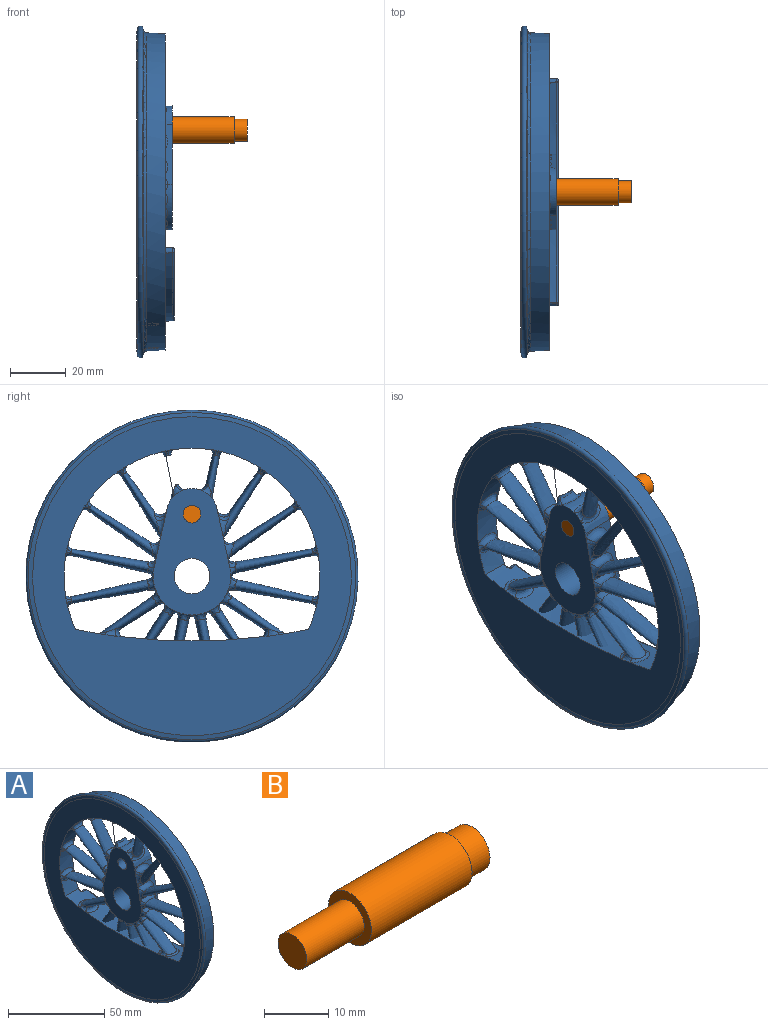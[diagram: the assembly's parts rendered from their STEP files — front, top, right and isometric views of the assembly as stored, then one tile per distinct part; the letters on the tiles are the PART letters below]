
ASSEMBLY  parts=2 mates=1
PART A: 135 faces, bbox 15.7x129.4x129.4 mm
  f0: cone r=9.16mm half-angle=2deg, axis (-1,0,0), area 176.3mm2, adj f1,f4,f129,f132,f133,f134
  f1: bspline ~10.76x6.08mm, area 60.7mm2, adj f0,f2,f3
  f2: bspline ~6.76x4.39mm, area 3.4mm2, adj f1,f3
  f3: bspline ~4.75x4.08mm, area 8.3mm2, adj f1,f2,f134
  f4: plane 21.3x12.7mm, normal (0.03,0.98,0.21), area 56.8mm2, adj f0,f5,f126,f127,f128,f129,f134
  f5: bspline ~11.82x11.44mm, area 83.1mm2, adj f4,f6,f7,f8,f9,f126
  f6: bspline ~4.14x3.37mm, area 6.3mm2, adj f5,f8,f9,f134
  f7: plane 1.45x1.08mm, normal (0.03,0.98,0.21), area 0.7mm2, adj f5,f126,f134
  f8: bspline ~6.9x3.29mm, area 11.8mm2, adj f5,f6,f9,f134
  f9: bspline ~23.53x17.18mm, area 361.5mm2, adj f5,f6,f8,f10,f125
  f10: bspline ~9.89x5.25mm, area 51.6mm2, adj f9,f11,f125
  f11: cone r=45.91mm half-angle=2deg, axis (1,0,0), area 1324.9mm2, adj f10,f12,f16,f19,f86,f87,f88,f112
  f12: bspline ~9.69x6.17mm, area 51.6mm2, adj f11,f13,f15
  f13: bspline ~15.19x7.22mm, area 197.8mm2, adj f12,f14,f15,f133
  f14: bspline ~4.75x4.08mm, area 8.3mm2, adj f13,f133,f134
  f15: bspline ~2.37x2.08mm, area 3.2mm2, adj f12,f13,f123
  f16: bspline ~9.69x6.17mm, area 51.6mm2, adj f11,f17,f18
  f17: bspline ~2.79x2.16mm, area 3.2mm2, adj f16,f18,f123
  f18: bspline ~6.39x2.51mm, area 1.6mm2, adj f16,f17
  f19: bspline ~9.89x5.24mm, area 51.6mm2, adj f11,f20,f21
  f20: bspline ~2.34x2.25mm, area 3.2mm2, adj f19,f21,f123
  f21: bspline ~25.72x18.68mm, area 455.8mm2, adj f19,f20,f22,f126
  f22: bspline ~7.22x3.59mm, area 11.9mm2, adj f21,f23,f126,f127,f134
  f23: bspline ~3.58x2.9mm, area 4.7mm2, adj f22,f24,f85,f127,f134
  f24: bspline ~28.93x8.8mm, area 483.4mm2, adj f23,f25,f84,f85,f86,f127
  f25: bspline ~11.52x4.62mm, area 34.3mm2, adj f24,f26,f85,f127,f128
  f26: bspline ~11.17x7.51mm, area 67.4mm2, adj f25,f27,f29,f83,f128
  f27: bspline ~28.93x8.8mm, area 486.9mm2, adj f26,f28,f83,f87
  f28: bspline ~2.37x2.08mm, area 3.2mm2, adj f27,f87,f123
  f29: bspline ~11.93x6.38mm, area 67.4mm2, adj f26,f30,f34,f82,f128
  f30: bspline ~21.12x15.67mm, area 345.6mm2, adj f29,f31,f32,f33,f82
  f31: bspline ~9.94x9.73mm, area 61.2mm2, adj f30,f32,f33,f119
  f32: bspline ~31.33x21.72mm, area 0mm2, adj f30,f31
  f33: bspline ~5.64x2.95mm, area 9.5mm2, adj f30,f31,f123
  f34: bspline ~11.68x6.38mm, area 67.4mm2, adj f29,f35,f80,f81,f128
  f35: bspline ~36.2x25.52mm, area 664.1mm2, adj f34,f36,f77,f81
  f36: cone r=56.77mm half-angle=2.8deg, axis (-1,0,0), area 6mm2, adj f35,f37
  f37: torus R=58.49mm, axis (-1,0,0), area 680mm2, adj f36,f38,f72,f73,f74,f77
  f38: cone r=56.77mm half-angle=2.8deg, axis (-1,0,0), area 6mm2, adj f37,f39
  f39: bspline ~41.37x10.96mm, area 664.1mm2, adj f38,f40,f77,f80
  f40: bspline ~5.5x3.18mm, area 8.8mm2, adj f39,f41,f80,f81,f134
  f41: bspline ~5.5x3.18mm, area 8.8mm2, adj f40,f42,f43,f71,f134
  f42: bspline ~41.37x10.96mm, area 664.1mm2, adj f41,f43,f72,f77
  f43: bspline ~11.68x7.51mm, area 67.4mm2, adj f41,f42,f44,f80,f128
  f44: bspline ~11.68x6.38mm, area 67.4mm2, adj f43,f45,f46,f71,f128
  f45: bspline ~36.2x25.52mm, area 664.1mm2, adj f44,f71,f73,f77
  f46: bspline ~11.93x6.38mm, area 67.4mm2, adj f44,f47,f50,f70,f128
  f47: bspline ~21.1x15.65mm, area 345.5mm2, adj f46,f48,f49,f70
  f48: bspline ~9.94x9.73mm, area 61.2mm2, adj f47,f49,f119
  f49: bspline ~5.29x2.96mm, area 9.5mm2, adj f47,f48,f123
  f50: bspline ~11.93x7.51mm, area 67.4mm2, adj f46,f51,f53,f69,f128
  f51: bspline ~28.93x8.8mm, area 486.9mm2, adj f50,f52,f69,f120
  f52: bspline ~2.79x2.11mm, area 3.2mm2, adj f51,f120,f123
  f53: bspline ~11.52x4.62mm, area 34.3mm2, adj f50,f54,f67,f68,f128
  f54: bspline ~28.93x8.8mm, area 483.4mm2, adj f53,f55,f66,f67,f68,f121
  f55: bspline ~3.58x2.9mm, area 4.7mm2, adj f54,f56,f67,f68,f134
  f56: bspline ~7.15x3.59mm, area 11.9mm2, adj f55,f57,f59,f68,f134
  f57: bspline ~25.72x18.68mm, area 455.7mm2, adj f56,f58,f59,f122
  f58: bspline ~2.34x2.25mm, area 3.2mm2, adj f57,f122,f123
  f59: bspline ~11.81x9.42mm, area 67.9mm2, adj f56,f57,f60,f65,f68,f132
  f60: bspline ~11.82x11.61mm, area 83.1mm2, adj f59,f61,f62,f63,f65,f132
  f61: bspline ~6.68x3.27mm, area 11.8mm2, adj f60,f62,f63,f134
  f62: bspline ~4.14x3.37mm, area 6.3mm2, adj f60,f61,f63,f134
  f63: bspline ~23.53x17.18mm, area 361.4mm2, adj f60,f61,f62,f64,f124
  f64: bspline ~2.54x2.44mm, area 3.2mm2, adj f63,f123,f124
  f65: plane 1.45x1.08mm, normal (0.03,-0.98,0.21), area 0.7mm2, adj f59,f60,f134
  f66: bspline ~2.37x2.08mm, area 3.2mm2, adj f54,f121,f123
  f67: bspline ~3.26x2.41mm, area 4.8mm2, adj f53,f54,f55,f69,f134
  f68: bspline ~11.75x4.6mm, area 29.7mm2, adj f53,f54,f55,f56,f59,f132
  f69: bspline ~5.5x3.18mm, area 8.8mm2, adj f50,f51,f67,f70,f134
  f70: bspline ~4.7x4.25mm, area 8.8mm2, adj f46,f47,f69,f71,f134
  f71: bspline ~4.7x4.25mm, area 8.8mm2, adj f41,f44,f45,f70,f134
  f72: cone r=56.77mm half-angle=2.8deg, axis (-1,0,0), area 6mm2, adj f37,f42
  f73: cone r=56.77mm half-angle=2.8deg, axis (-1,0,0), area 6mm2, adj f37,f45
  f74: cone r=58.25mm half-angle=80deg, axis (-1,0,0), area 168mm2, adj f37,f75
  f75: torus R=58.52mm, axis (-1,0,0), area 1056mm2, adj f74,f76
  f76: cone r=57.15mm half-angle=80deg, axis (1,0,0), area 572.1mm2, adj f75,f123
  f77: cone r=56.77mm half-angle=2.8deg, axis (-1,0,0), area 2387.5mm2, adj f35,f37,f39,f42,f45,f78
  f78: plane 113.53x113.53mm, normal (1,0,0), area 2217.4mm2, adj f77,f79
  f79: cylinder r=50.16mm len=100.33mm, axis (-1,0,0), area 128.1mm2, adj f78,f114
  f80: bspline ~11.68x7.52mm, area 67.4mm2, adj f34,f39,f40,f43,f128
  f81: bspline ~4.7x4.25mm, area 8.8mm2, adj f34,f35,f40,f82,f134
  f82: bspline ~4.7x4.25mm, area 8.8mm2, adj f29,f30,f81,f83,f134
  f83: bspline ~5.5x3.18mm, area 8.8mm2, adj f26,f27,f82,f85,f134
  f84: bspline ~2.79x2.11mm, area 3.2mm2, adj f24,f86,f123
  f85: bspline ~3.26x2.41mm, area 4.8mm2, adj f23,f24,f25,f83,f134
  f86: bspline ~9.89x6.18mm, area 51.6mm2, adj f11,f24,f84
  f87: bspline ~9.89x6.18mm, area 51.6mm2, adj f11,f27,f28
  f88: torus R=203.57mm, axis (1,0,0), area 1mm2, adj f11,f89,f111,f112,f119
  f89: plane 0.9x0.88mm, normal (1,0,0), area 0.3mm2, adj f88,f90,f112
  f90: torus R=2.1mm, axis (1,0,0), area 1.5mm2, adj f89,f91,f110,f111,f113
  f91: cylinder r=1.59mm len=2.57mm, axis (-1,0,0), area 6.6mm2, adj f90,f92,f108,f109
  f92: bspline ~4.2x0.69mm, area 0.4mm2, adj f91,f93,f110,f115
  f93: sphere r=0.51mm, area 0.1mm2, adj f92,f94,f108
  f94: torus R=45.64mm, axis (1,0,0), area 77.5mm2, adj f93,f95,f107,f115
  f95: sphere r=0.51mm, area 0.1mm2, adj f94,f96,f106
  f96: torus R=1.08mm, axis (1,0,0), area 1.3mm2, adj f95,f97,f103,f107
  f97: cylinder r=1.59mm len=2.57mm, axis (-1,0,0), area 5.6mm2, adj f96,f98,f100,f106
  f98: bspline ~5.46x0.69mm, area 0.8mm2, adj f97,f99,f103,f119
  f99: bspline ~1.57x1.15mm, area 0.8mm2, adj f98,f100,f118,f119
  f100: torus R=2.1mm, axis (1,0,0), area 1.3mm2, adj f97,f99,f101,f102,f116
  f101: plane 0.77x0.73mm, normal (1,0,0), area 0.2mm2, adj f100,f117,f118
  f102: bspline ~0.78x0.75mm, area 0.1mm2, adj f100,f106,f115,f116
  f103: sphere r=0.51mm, area 0.2mm2, adj f96,f98,f104
  f104: torus R=203.69mm, axis (1,0,0), area 62mm2, adj f103,f105,f107,f119
  f105: sphere r=0.51mm, area 0.1mm2, adj f104,f108,f109
  f106: bspline ~4.2x0.69mm, area 0.4mm2, adj f95,f97,f102,f115
  f107: plane 80.51x25.21mm, normal (1,0,0), area 1263.4mm2, adj f94,f96,f104,f108
  f108: torus R=1.08mm, axis (1,0,0), area 1.5mm2, adj f91,f93,f105,f107
  f109: bspline ~4.25x0.7mm, area 0.4mm2, adj f91,f105,f111,f119
  f110: bspline ~0.77x0.72mm, area 0.1mm2, adj f90,f92,f113,f115
  f111: bspline ~1.69x1.07mm, area 0.8mm2, adj f88,f90,f109,f119
  f112: torus R=46.08mm, axis (-1,0,0), area 0.2mm2, adj f11,f88,f89,f113
  f113: bspline ~1.18x0.58mm, area 0.2mm2, adj f11,f90,f110,f112
  f114: plane 100.33x100.33mm, normal (1,0,0), area 1184mm2, adj f11,f79
  f115: cone r=46.13mm half-angle=2deg, axis (-1,0,0), area 310.9mm2, adj f11,f92,f94,f102,f106,f110
  f116: bspline ~1.18x0.58mm, area 0.2mm2, adj f11,f100,f102,f117
  f117: torus R=46.08mm, axis (-1,0,0), area 0.2mm2, adj f11,f101,f116,f118
  f118: torus R=203.57mm, axis (1,0,0), area 0.9mm2, adj f11,f99,f101,f117,f119
  f119: cone r=203.2mm half-angle=2deg, axis (1,0,0), area 916.8mm2, adj f11,f31,f48,f88,f98,f99,f104,f109
  f120: bspline ~9.89x6.18mm, area 51.6mm2, adj f11,f51,f52
  f121: bspline ~9.89x6.18mm, area 51.6mm2, adj f11,f54,f66
  f122: bspline ~9.89x5.25mm, area 51.6mm2, adj f11,f57,f58
  f123: plane 114.38x114.38mm, normal (-1,0,0), area 5011.9mm2, adj f11,f15,f17,f20,f28,f33,f49,f52
  f124: bspline ~9.89x5.24mm, area 51.6mm2, adj f11,f63,f64
  f125: bspline ~2.53x2.41mm, area 3.2mm2, adj f9,f10,f123
  f126: bspline ~11.67x9.42mm, area 67.9mm2, adj f4,f5,f7,f21,f22,f127
  f127: bspline ~11.75x4.6mm, area 29.7mm2, adj f4,f22,f23,f24,f25,f126
  f128: cone r=13.93mm half-angle=2deg, axis (-1,0,0), area 98.8mm2, adj f4,f25,f26,f29,f34,f43,f44,f46
  f129: plane 44.43x26.98mm, normal (1,0,0), area 751.8mm2, adj f0,f4,f128,f130,f131,f132
  f130: cylinder r=3.17mm len=12.7mm, axis (1,0,0), area 253.4mm2, adj f129,f134
  f131: cylinder r=6.35mm len=12.7mm, axis (1,0,0), area 506.7mm2, adj f129,f134
  f132: plane 21.3x12.7mm, normal (0.03,-0.98,0.21), area 56.8mm2, adj f0,f59,f60,f68,f128,f129,f134
  f133: bspline ~10.76x6.08mm, area 60.7mm2, adj f0,f13,f14
  f134: plane 45.87x28.41mm, normal (-1,0,0), area 803.6mm2, adj f0,f3,f4,f6,f7,f8,f14,f22
PART B: 7 faces, bbox 39.7x9.5x9.5 mm
  f0: cylinder r=3.17mm len=12.7mm, axis (1,0,0), area 253.4mm2, adj f1,f6
  f1: plane 6.35x6.35mm, normal (-1,0,0), area 31.7mm2, adj f0
  f2: plane 7.94x7.94mm, normal (1,0,0), area 49.5mm2, adj f3
  f3: cylinder r=3.97mm len=7.94mm, axis (1,0,0), area 118.8mm2, adj f2,f4
  f4: plane 9.53x9.53mm, normal (1,0,0), area 21.8mm2, adj f3,f5
  f5: cylinder r=4.76mm len=22.23mm, axis (1,0,0), area 665.1mm2, adj f4,f6
  f6: plane 9.53x9.53mm, normal (-1,0,0), area 39.6mm2, adj f0,f5
PLACE A t=(-31.66,-30.25,-57.37)mm
PLACE B t=(-18.96,-30.25,-35.15)mm
MATE fastened A.f0 <-> B.f0  axis (1,0,0) through (-18.96,-30.25,-35.15)mm
